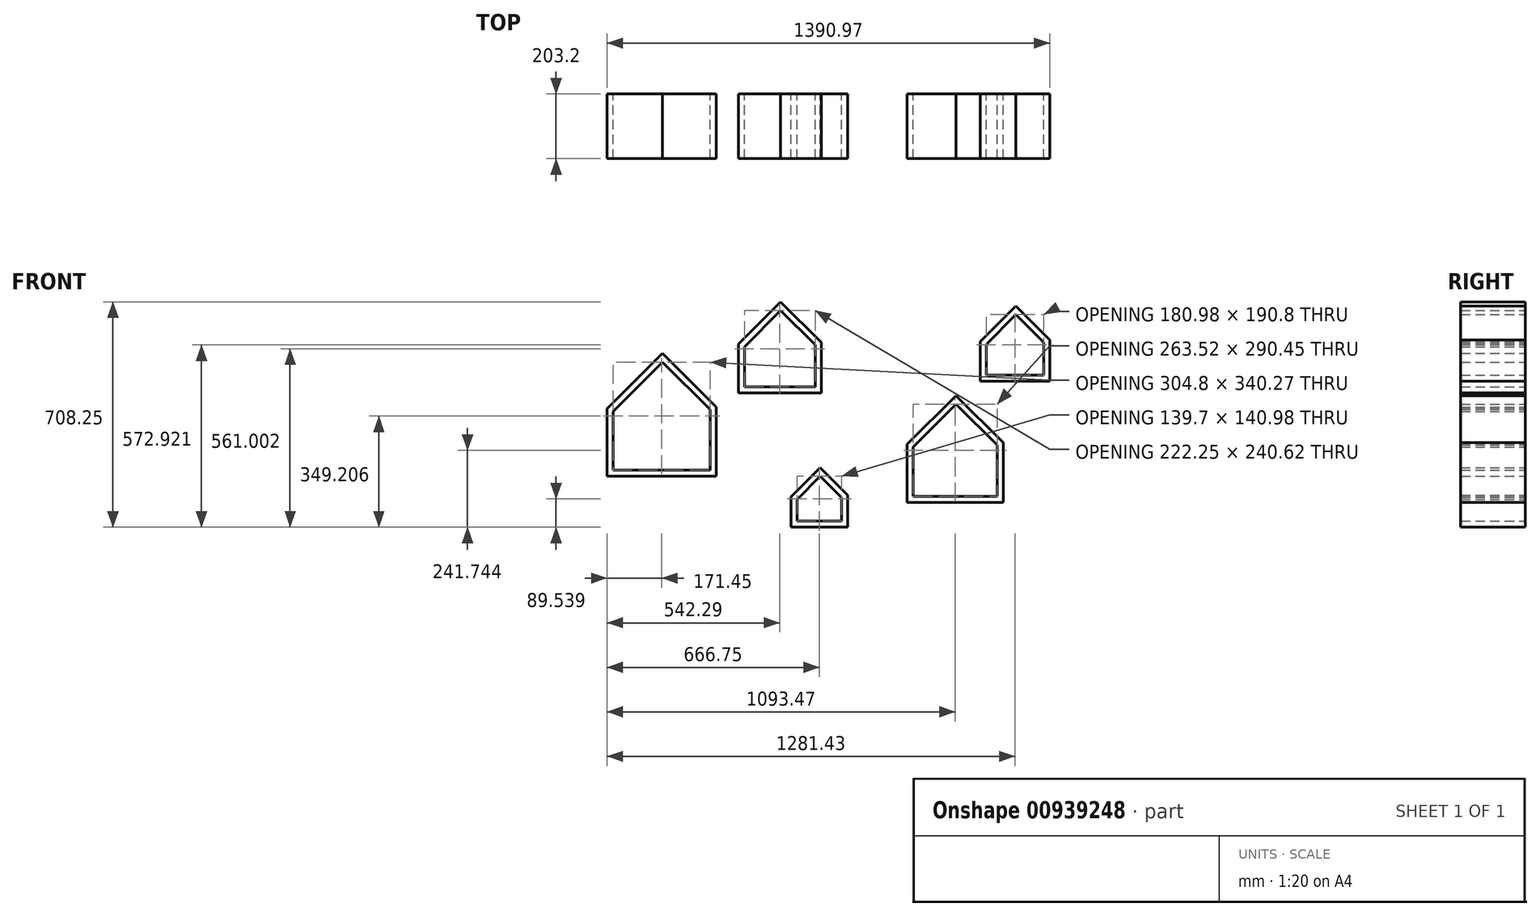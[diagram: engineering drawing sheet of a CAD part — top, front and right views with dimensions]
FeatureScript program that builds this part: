
annotation { "Feature Type Name" : "Feature", "Feature Type Description" : "" }
export const myFeature = defineFeature(function(context is Context, id is Id, definition is map)
    precondition{}
    {
        {
            var Q0;
            Q0=qCreatedBy(makeId("Front.planeOp"),FACE);
            var sketch = newSketch(context, id + "F0", { "sketchPlane" : qUnion([Q0])});
            skLineSegment(sketch, "E0.left", {"start": v(-274.9, 280.82) * mm, "end": v(-274.9, 95.58) * mm});
            skLineSegment(sketch, "E0.right", {"start": v(29.9, 286.08) * mm, "end": v(29.9, 95.58) * mm});
            skLineSegment(sketch, "E1", {"start": v(-119.86, 435.85) * mm, "end": v(-274.9, 280.82) * mm});
            skLineSegment(sketch, "E2", {"start": v(29.9, 286.08) * mm, "end": v(-119.86, 435.85) * mm});
            skPoint(sketch, "E3.start.orphan", {"position": v(-122.5, 283.45) * mm});
            skLineSegment(sketch, "E4", {"start": v(-274.9, 95.58) * mm, "end": v(29.9, 95.58) * mm});
            skLineSegment(sketch, "E5.0", {"start": v(48.96, 293.97) * mm, "end": v(48.96, 76.53) * mm});
            skLineSegment(sketch, "E5.1", {"start": v(-293.94, 76.53) * mm, "end": v(48.96, 76.53) * mm});
            skLineSegment(sketch, "E5.2", {"start": v(48.96, 293.97) * mm, "end": v(-119.86, 462.8) * mm});
            skLineSegment(sketch, "E5.3", {"start": v(-119.86, 462.8) * mm, "end": v(-293.94, 288.71) * mm});
            skLineSegment(sketch, "E5.4", {"start": v(-293.94, 288.71) * mm, "end": v(-293.94, 76.53) * mm});
            skLineSegment(sketch, "E6.0", {"start": v(-119.86, 433.6) * mm, "end": v(-273.3, 280.16) * mm});
            skLineSegment(sketch, "E6.1", {"start": v(28.32, 285.42) * mm, "end": v(-119.86, 433.6) * mm});
            skLineSegment(sketch, "E6.2", {"start": v(-273.3, 280.16) * mm, "end": v(-273.3, 97.17) * mm});
            skLineSegment(sketch, "E6.3", {"start": v(-273.3, 97.17) * mm, "end": v(28.32, 97.17) * mm});
            skLineSegment(sketch, "E6.4", {"start": v(28.32, 285.42) * mm, "end": v(28.32, 97.17) * mm});
            skLineSegment(sketch, "E7.0", {"start": v(-119.86, 406.66) * mm, "end": v(-254.25, 272.27) * mm});
            skLineSegment(sketch, "E7.1", {"start": v(9.27, 277.53) * mm, "end": v(-119.86, 406.66) * mm});
            skLineSegment(sketch, "E7.2", {"start": v(-254.25, 272.27) * mm, "end": v(-254.25, 116.22) * mm});
            skLineSegment(sketch, "E7.3", {"start": v(-254.25, 116.22) * mm, "end": v(9.27, 116.22) * mm});
            skLineSegment(sketch, "E7.4", {"start": v(9.27, 277.53) * mm, "end": v(9.27, 116.22) * mm});
            skLineSegment(sketch, "E8.0", {"start": v(-252.67, 271.61) * mm, "end": v(-252.67, 117.8) * mm});
            skLineSegment(sketch, "E8.1", {"start": v(-119.86, 404.42) * mm, "end": v(-252.67, 271.61) * mm});
            skLineSegment(sketch, "E8.2", {"start": v(-252.67, 117.8) * mm, "end": v(7.68, 117.8) * mm});
            skLineSegment(sketch, "E8.3", {"start": v(7.68, 276.87) * mm, "end": v(7.68, 117.8) * mm});
            skLineSegment(sketch, "E8.4", {"start": v(7.68, 276.87) * mm, "end": v(-119.86, 404.42) * mm});
            skLineSegment(sketch, "E9.0", {"start": v(-233.62, 263.72) * mm, "end": v(-233.62, 136.86) * mm});
            skLineSegment(sketch, "E9.1", {"start": v(-119.86, 377.48) * mm, "end": v(-233.62, 263.72) * mm});
            skLineSegment(sketch, "E9.2", {"start": v(-233.62, 136.86) * mm, "end": v(-11.37, 136.86) * mm});
            skLineSegment(sketch, "E9.3", {"start": v(-11.37, 268.98) * mm, "end": v(-11.37, 136.86) * mm});
            skLineSegment(sketch, "E9.4", {"start": v(-11.37, 268.98) * mm, "end": v(-119.86, 377.48) * mm});
            skLineSegment(sketch, "E10.0", {"start": v(-232.03, 263.07) * mm, "end": v(-232.03, 138.44) * mm});
            skLineSegment(sketch, "E10.1", {"start": v(-119.86, 375.23) * mm, "end": v(-232.03, 263.07) * mm});
            skLineSegment(sketch, "E10.2", {"start": v(-232.03, 138.44) * mm, "end": v(-12.95, 138.44) * mm});
            skLineSegment(sketch, "E10.3", {"start": v(-12.95, 268.33) * mm, "end": v(-12.95, 138.44) * mm});
            skLineSegment(sketch, "E10.4", {"start": v(-12.95, 268.33) * mm, "end": v(-119.86, 375.23) * mm});
            skLineSegment(sketch, "E11.0", {"start": v(-212.98, 255.18) * mm, "end": v(-212.98, 157.5) * mm});
            skLineSegment(sketch, "E11.1", {"start": v(-119.86, 348.3) * mm, "end": v(-212.98, 255.18) * mm});
            skLineSegment(sketch, "E11.2", {"start": v(-212.98, 157.5) * mm, "end": v(-32, 157.5) * mm});
            skLineSegment(sketch, "E11.3", {"start": v(-32, 260.44) * mm, "end": v(-32, 157.5) * mm});
            skLineSegment(sketch, "E11.4", {"start": v(-32, 260.44) * mm, "end": v(-119.86, 348.3) * mm});
            skLineSegment(sketch, "E12.0", {"start": v(-211.4, 254.52) * mm, "end": v(-211.4, 159.08) * mm});
            skLineSegment(sketch, "E12.1", {"start": v(-119.86, 346.05) * mm, "end": v(-211.4, 254.52) * mm});
            skLineSegment(sketch, "E12.2", {"start": v(-211.4, 159.08) * mm, "end": v(-33.6, 159.08) * mm});
            skLineSegment(sketch, "E12.3", {"start": v(-33.6, 259.78) * mm, "end": v(-33.6, 159.08) * mm});
            skLineSegment(sketch, "E12.4", {"start": v(-33.6, 259.78) * mm, "end": v(-119.86, 346.05) * mm});
            skLineSegment(sketch, "E13.0", {"start": v(-192.34, 246.63) * mm, "end": v(-192.34, 178.13) * mm});
            skLineSegment(sketch, "E13.1", {"start": v(-119.86, 319.1) * mm, "end": v(-192.34, 246.63) * mm});
            skLineSegment(sketch, "E13.2", {"start": v(-192.34, 178.13) * mm, "end": v(-52.64, 178.13) * mm});
            skLineSegment(sketch, "E13.3", {"start": v(-52.64, 251.89) * mm, "end": v(-52.64, 178.13) * mm});
            skLineSegment(sketch, "E13.4", {"start": v(-52.64, 251.89) * mm, "end": v(-119.86, 319.1) * mm});
            skSolve(sketch);
        }
        {
            var Q0;
            Q0=makeQuery(id+"F0.imprint","IMPRINT",FACE,{"disambiguationData":[TD([[makeQuery(id+"F0.imprint","IMPRINT",EDGE,{"derivedFrom":sQuery(id+"F0.wireOp",EDGE,"E0.left")}),-1.0]])]});
            var Q1;
            Q1=makeQuery(id+"F0.imprint","IMPRINT",FACE,{"disambiguationData":[TD([[makeQuery(id+"F0.imprint","IMPRINT",EDGE,{"derivedFrom":sQuery(id+"F0.wireOp",EDGE,"E6.0")}),1.0]])]});
            var Q2;
            Q2=makeQuery(id+"F0.imprint","IMPRINT",FACE,{"disambiguationData":[TD([[makeQuery(id+"F0.imprint","IMPRINT",EDGE,{"derivedFrom":sQuery(id+"F0.wireOp",EDGE,"E8.0")}),1.0]])]});
            var Q3;
            Q3=makeQuery(id+"F0.imprint","IMPRINT",FACE,{"disambiguationData":[TD([[makeQuery(id+"F0.imprint","IMPRINT",EDGE,{"derivedFrom":sQuery(id+"F0.wireOp",EDGE,"E10.0")}),1.0]])]});
            var Q4;
            Q4=makeQuery(id+"F0.imprint","IMPRINT",FACE,{"disambiguationData":[TD([[makeQuery(id+"F0.imprint","IMPRINT",EDGE,{"derivedFrom":sQuery(id+"F0.wireOp",EDGE,"E12.0")}),1.0]])]});
            extrude(context, id + "F1", {"entities" : qUnion([Q0, Q1, Q2, Q3, Q4]), "depth" : 203.2 * mm, "offsetDistance" : 25.4 * mm});
        }
        {
            var Q0;
            Q0=makeQuery(id+"F1.opExtrude","CAP_EDGE",EDGE,{"disambiguationData":[OSD([sQuery(id+"F0.wireOp",EDGE,"E6.3")])],"isStart":false});
            cPoint(context, id + "F2", {"entities" : qUnion([Q0]), "parameter" : 0.5});
        }
        {
            var Q0;
            Q0=makeQuery(id+"F1.opExtrude","CAP_EDGE",EDGE,{"disambiguationData":[OSD([sQuery(id+"F0.wireOp",EDGE,"E4")])],"isStart":false});
            cPoint(context, id + "F3", {"entities" : qUnion([Q0]), "parameter" : 0.5});
        }
        {
            var Q0;
            Q0=makeQuery(id+"F1.opExtrude","SWEPT_BODY",BODY,{"disambiguationData":[OSD([sQuery(id+"F0.wireOp",EDGE,"E6.0"),sQuery(id+"F0.wireOp",EDGE,"E6.1"),sQuery(id+"F0.wireOp",EDGE,"E6.2"),sQuery(id+"F0.wireOp",EDGE,"E6.3"),sQuery(id+"F0.wireOp",EDGE,"E6.4"),sQuery(id+"F0.wireOp",EDGE,"E7.0"),sQuery(id+"F0.wireOp",EDGE,"E7.1"),sQuery(id+"F0.wireOp",EDGE,"E7.2"),sQuery(id+"F0.wireOp",EDGE,"E7.3"),sQuery(id+"F0.wireOp",EDGE,"E7.4")])]});
            var Q1;
            Q1 = qCreatedBy(id + "F2" ,VERTEX);
            var Q2;
            Q2 = qCreatedBy(id + "F3" ,VERTEX);
            transform(context, id + "F4", {"entities" : qUnion([Q0]), "transformType" : TransformType.TRANSLATION_ENTITY, "oppositeDirectionEntity" : false, "transformLine" : qUnion([Q1, Q2]), "makeCopy" : false});
        }
        {
            var Q0;
            Q0=makeQuery(id+"F1.opExtrude","CAP_EDGE",EDGE,{"disambiguationData":[OSD([sQuery(id+"F0.wireOp",EDGE,"E8.2")])],"isStart":false});
            cPoint(context, id + "F5", {"entities" : qUnion([Q0]), "parameter" : 0.5});
        }
        {
            var Q0;
            Q0=makeQuery(id+"F1.opExtrude","CAP_EDGE",EDGE,{"disambiguationData":[OSD([sQuery(id+"F0.wireOp",EDGE,"E7.3")])],"isStart":false});
            cPoint(context, id + "F6", {"entities" : qUnion([Q0]), "parameter" : 0.5});
        }
        {
            var Q0;
            Q0=makeQuery(id+"F1.opExtrude","SWEPT_BODY",BODY,{"disambiguationData":[OSD([sQuery(id+"F0.wireOp",EDGE,"E8.0"),sQuery(id+"F0.wireOp",EDGE,"E8.1"),sQuery(id+"F0.wireOp",EDGE,"E8.2"),sQuery(id+"F0.wireOp",EDGE,"E8.3"),sQuery(id+"F0.wireOp",EDGE,"E8.4"),sQuery(id+"F0.wireOp",EDGE,"E9.0"),sQuery(id+"F0.wireOp",EDGE,"E9.1"),sQuery(id+"F0.wireOp",EDGE,"E9.2"),sQuery(id+"F0.wireOp",EDGE,"E9.3"),sQuery(id+"F0.wireOp",EDGE,"E9.4")])]});
            var Q1;
            Q1 = qCreatedBy(id + "F5" ,VERTEX);
            var Q2;
            Q2 = qCreatedBy(id + "F6" ,VERTEX);
            transform(context, id + "F7", {"entities" : qUnion([Q0]), "transformType" : TransformType.TRANSLATION_ENTITY, "oppositeDirectionEntity" : false, "transformLine" : qUnion([Q1, Q2]), "makeCopy" : false});
        }
        {
            var Q0;
            Q0=makeQuery(id+"F1.opExtrude","CAP_EDGE",EDGE,{"disambiguationData":[OSD([sQuery(id+"F0.wireOp",EDGE,"E10.2")])],"isStart":false});
            cPoint(context, id + "F8", {"entities" : qUnion([Q0]), "parameter" : 0.5});
        }
        {
            var Q0;
            Q0=makeQuery(id+"F1.opExtrude","CAP_EDGE",EDGE,{"disambiguationData":[OSD([sQuery(id+"F0.wireOp",EDGE,"E9.2")])],"isStart":false});
            cPoint(context, id + "F9", {"entities" : qUnion([Q0]), "parameter" : 0.5});
        }
        {
            var Q0;
            Q0=makeQuery(id+"F1.opExtrude","SWEPT_BODY",BODY,{"disambiguationData":[OSD([sQuery(id+"F0.wireOp",EDGE,"E10.0"),sQuery(id+"F0.wireOp",EDGE,"E10.1"),sQuery(id+"F0.wireOp",EDGE,"E10.2"),sQuery(id+"F0.wireOp",EDGE,"E10.3"),sQuery(id+"F0.wireOp",EDGE,"E10.4"),sQuery(id+"F0.wireOp",EDGE,"E11.0"),sQuery(id+"F0.wireOp",EDGE,"E11.1"),sQuery(id+"F0.wireOp",EDGE,"E11.2"),sQuery(id+"F0.wireOp",EDGE,"E11.3"),sQuery(id+"F0.wireOp",EDGE,"E11.4")])]});
            var Q1;
            Q1 = qCreatedBy(id + "F8" ,VERTEX);
            var Q2;
            Q2 = qCreatedBy(id + "F9" ,VERTEX);
            transform(context, id + "F10", {"entities" : qUnion([Q0]), "transformType" : TransformType.TRANSLATION_ENTITY, "oppositeDirectionEntity" : false, "transformLine" : qUnion([Q1, Q2]), "makeCopy" : false});
        }
        {
            var Q0;
            Q0=makeQuery(id+"F1.opExtrude","CAP_EDGE",EDGE,{"disambiguationData":[OSD([sQuery(id+"F0.wireOp",EDGE,"E12.2")])],"isStart":false});
            cPoint(context, id + "F11", {"entities" : qUnion([Q0]), "parameter" : 0.5});
        }
        {
            var Q0;
            Q0=makeQuery(id+"F1.opExtrude","CAP_EDGE",EDGE,{"disambiguationData":[OSD([sQuery(id+"F0.wireOp",EDGE,"E11.2")])],"isStart":false});
            cPoint(context, id + "F12", {"entities" : qUnion([Q0]), "parameter" : 0.5});
        }
        {
            var Q0;
            Q0=makeQuery(id+"F1.opExtrude","SWEPT_BODY",BODY,{"disambiguationData":[OSD([sQuery(id+"F0.wireOp",EDGE,"E12.0"),sQuery(id+"F0.wireOp",EDGE,"E12.1"),sQuery(id+"F0.wireOp",EDGE,"E12.2"),sQuery(id+"F0.wireOp",EDGE,"E12.3"),sQuery(id+"F0.wireOp",EDGE,"E12.4"),sQuery(id+"F0.wireOp",EDGE,"E13.0"),sQuery(id+"F0.wireOp",EDGE,"E13.1"),sQuery(id+"F0.wireOp",EDGE,"E13.2"),sQuery(id+"F0.wireOp",EDGE,"E13.3"),sQuery(id+"F0.wireOp",EDGE,"E13.4")])]});
            var Q1;
            Q1 = qCreatedBy(id + "F11" ,VERTEX);
            var Q2;
            Q2 = qCreatedBy(id + "F12" ,VERTEX);
            transform(context, id + "F13", {"entities" : qUnion([Q0]), "transformType" : TransformType.TRANSLATION_ENTITY, "oppositeDirectionEntity" : false, "transformLine" : qUnion([Q1, Q2]), "makeCopy" : false});
        }
        {
            var Q0;
            Q0=makeQuery(id+"F1.opExtrude","SWEPT_BODY",BODY,{"disambiguationData":[OSD([sQuery(id+"F0.wireOp",EDGE,"E12.0"),sQuery(id+"F0.wireOp",EDGE,"E12.1"),sQuery(id+"F0.wireOp",EDGE,"E12.2"),sQuery(id+"F0.wireOp",EDGE,"E12.3"),sQuery(id+"F0.wireOp",EDGE,"E12.4"),sQuery(id+"F0.wireOp",EDGE,"E13.0"),sQuery(id+"F0.wireOp",EDGE,"E13.1"),sQuery(id+"F0.wireOp",EDGE,"E13.2"),sQuery(id+"F0.wireOp",EDGE,"E13.3"),sQuery(id+"F0.wireOp",EDGE,"E13.4")])]});
            transform(context, id + "F14", {"entities" : qUnion([Q0]), "transformType" : TransformType.TRANSLATION_3D, "dx" : 546.1 * mm, "dy" : 0 * mm, "dz" : 208.28 * mm, "makeCopy" : false});
        }
        {
            var Q0;
            Q0=makeQuery(id+"F1.opExtrude","SWEPT_BODY",BODY,{"disambiguationData":[OSD([sQuery(id+"F0.wireOp",EDGE,"E10.0"),sQuery(id+"F0.wireOp",EDGE,"E10.1"),sQuery(id+"F0.wireOp",EDGE,"E10.2"),sQuery(id+"F0.wireOp",EDGE,"E10.3"),sQuery(id+"F0.wireOp",EDGE,"E10.4"),sQuery(id+"F0.wireOp",EDGE,"E11.0"),sQuery(id+"F0.wireOp",EDGE,"E11.1"),sQuery(id+"F0.wireOp",EDGE,"E11.2"),sQuery(id+"F0.wireOp",EDGE,"E11.3"),sQuery(id+"F0.wireOp",EDGE,"E11.4")])]});
            transform(context, id + "F15", {"entities" : qUnion([Q0]), "transformType" : TransformType.TRANSLATION_3D, "dx" : 454.66 * mm, "dy" : 0 * mm, "dz" : -302.26 * mm, "makeCopy" : false});
        }
        {
            var Q0;
            Q0=makeQuery(id+"F1.opExtrude","SWEPT_BODY",BODY,{"disambiguationData":[OSD([sQuery(id+"F0.wireOp",EDGE,"E8.0"),sQuery(id+"F0.wireOp",EDGE,"E8.1"),sQuery(id+"F0.wireOp",EDGE,"E8.2"),sQuery(id+"F0.wireOp",EDGE,"E8.3"),sQuery(id+"F0.wireOp",EDGE,"E8.4"),sQuery(id+"F0.wireOp",EDGE,"E9.0"),sQuery(id+"F0.wireOp",EDGE,"E9.1"),sQuery(id+"F0.wireOp",EDGE,"E9.2"),sQuery(id+"F0.wireOp",EDGE,"E9.3"),sQuery(id+"F0.wireOp",EDGE,"E9.4")])]});
            transform(context, id + "F16", {"entities" : qUnion([Q0]), "transformType" : TransformType.TRANSLATION_3D, "dx" : 756.92 * mm, "dy" : 0 * mm, "dz" : 0 * mm, "makeCopy" : false});
        }
        {
            var Q0;
            Q0=makeQuery(id+"F1.opExtrude","SWEPT_BODY",BODY,{"disambiguationData":[OSD([sQuery(id+"F0.wireOp",EDGE,"E6.0"),sQuery(id+"F0.wireOp",EDGE,"E6.1"),sQuery(id+"F0.wireOp",EDGE,"E6.2"),sQuery(id+"F0.wireOp",EDGE,"E6.3"),sQuery(id+"F0.wireOp",EDGE,"E6.4"),sQuery(id+"F0.wireOp",EDGE,"E7.0"),sQuery(id+"F0.wireOp",EDGE,"E7.1"),sQuery(id+"F0.wireOp",EDGE,"E7.2"),sQuery(id+"F0.wireOp",EDGE,"E7.3"),sQuery(id+"F0.wireOp",EDGE,"E7.4")])]});
            transform(context, id + "F17", {"entities" : qUnion([Q0]), "transformType" : TransformType.TRANSLATION_3D, "dx" : -457.2 * mm, "dy" : 0 * mm, "dz" : 162.56 * mm, "makeCopy" : false});
        }
        {
            var Q0;
            Q0=makeQuery(id+"F1.opExtrude","SWEPT_BODY",BODY,{"disambiguationData":[OSD([sQuery(id+"F0.wireOp",EDGE,"E6.0"),sQuery(id+"F0.wireOp",EDGE,"E6.1"),sQuery(id+"F0.wireOp",EDGE,"E6.2"),sQuery(id+"F0.wireOp",EDGE,"E6.3"),sQuery(id+"F0.wireOp",EDGE,"E6.4"),sQuery(id+"F0.wireOp",EDGE,"E7.0"),sQuery(id+"F0.wireOp",EDGE,"E7.1"),sQuery(id+"F0.wireOp",EDGE,"E7.2"),sQuery(id+"F0.wireOp",EDGE,"E7.3"),sQuery(id+"F0.wireOp",EDGE,"E7.4")])]});
            transform(context, id + "F18", {"entities" : qUnion([Q0]), "transformType" : TransformType.TRANSLATION_3D, "dx" : 1379.22 * mm, "dy" : 0 * mm, "dz" : -264.16 * mm, "makeCopy" : false});
        }
        {
            var Q0;
            Q0=makeQuery(id+"F1.opExtrude","SWEPT_BODY",BODY,{"disambiguationData":[OSD([sQuery(id+"F0.wireOp",EDGE,"E10.0"),sQuery(id+"F0.wireOp",EDGE,"E10.1"),sQuery(id+"F0.wireOp",EDGE,"E10.2"),sQuery(id+"F0.wireOp",EDGE,"E10.3"),sQuery(id+"F0.wireOp",EDGE,"E10.4"),sQuery(id+"F0.wireOp",EDGE,"E11.0"),sQuery(id+"F0.wireOp",EDGE,"E11.1"),sQuery(id+"F0.wireOp",EDGE,"E11.2"),sQuery(id+"F0.wireOp",EDGE,"E11.3"),sQuery(id+"F0.wireOp",EDGE,"E11.4")])]});
            transform(context, id + "F19", {"entities" : qUnion([Q0]), "transformType" : TransformType.TRANSLATION_3D, "dx" : -119.38 * mm, "dy" : 0 * mm, "dz" : 33.02 * mm, "makeCopy" : false});
        }
        {
            var Q0;
            Q0=makeQuery(id+"F1.opExtrude","SWEPT_BODY",BODY,{"disambiguationData":[OSD([sQuery(id+"F0.wireOp",EDGE,"E12.0"),sQuery(id+"F0.wireOp",EDGE,"E12.1"),sQuery(id+"F0.wireOp",EDGE,"E12.2"),sQuery(id+"F0.wireOp",EDGE,"E12.3"),sQuery(id+"F0.wireOp",EDGE,"E12.4"),sQuery(id+"F0.wireOp",EDGE,"E13.0"),sQuery(id+"F0.wireOp",EDGE,"E13.1"),sQuery(id+"F0.wireOp",EDGE,"E13.2"),sQuery(id+"F0.wireOp",EDGE,"E13.3"),sQuery(id+"F0.wireOp",EDGE,"E13.4")])]});
            transform(context, id + "F20", {"entities" : qUnion([Q0]), "transformType" : TransformType.TRANSLATION_3D, "dx" : 157.48 * mm, "dy" : 0 * mm, "dz" : 0 * mm, "makeCopy" : false});
        }
        {
            var Q0;
            Q0=makeQuery(id+"F1.opExtrude","SWEPT_BODY",BODY,{"disambiguationData":[OSD([sQuery(id+"F0.wireOp",EDGE,"E8.0"),sQuery(id+"F0.wireOp",EDGE,"E8.1"),sQuery(id+"F0.wireOp",EDGE,"E8.2"),sQuery(id+"F0.wireOp",EDGE,"E8.3"),sQuery(id+"F0.wireOp",EDGE,"E8.4"),sQuery(id+"F0.wireOp",EDGE,"E9.0"),sQuery(id+"F0.wireOp",EDGE,"E9.1"),sQuery(id+"F0.wireOp",EDGE,"E9.2"),sQuery(id+"F0.wireOp",EDGE,"E9.3"),sQuery(id+"F0.wireOp",EDGE,"E9.4")])]});
            transform(context, id + "F21", {"entities" : qUnion([Q0]), "transformType" : TransformType.TRANSLATION_3D, "dx" : -386.08 * mm, "dy" : 0 * mm, "dz" : 223.52 * mm, "makeCopy" : false});
        }
        {
            var Q0;
            Q0=makeQuery(id+"F1.opExtrude","SWEPT_BODY",BODY,{"disambiguationData":[OSD([sQuery(id+"F0.wireOp",EDGE,"E12.0"),sQuery(id+"F0.wireOp",EDGE,"E12.1"),sQuery(id+"F0.wireOp",EDGE,"E12.2"),sQuery(id+"F0.wireOp",EDGE,"E12.3"),sQuery(id+"F0.wireOp",EDGE,"E12.4"),sQuery(id+"F0.wireOp",EDGE,"E13.0"),sQuery(id+"F0.wireOp",EDGE,"E13.1"),sQuery(id+"F0.wireOp",EDGE,"E13.2"),sQuery(id+"F0.wireOp",EDGE,"E13.3"),sQuery(id+"F0.wireOp",EDGE,"E13.4")])]});
            transform(context, id + "F22", {"entities" : qUnion([Q0]), "transformType" : TransformType.TRANSLATION_3D, "dx" : -208.28 * mm, "dy" : 0 * mm, "dz" : -340.36 * mm, "makeCopy" : false});
        }
        {
            var Q0;
            Q0=makeQuery(id+"F1.opExtrude","SWEPT_BODY",BODY,{"disambiguationData":[OSD([sQuery(id+"F0.wireOp",EDGE,"E10.0"),sQuery(id+"F0.wireOp",EDGE,"E10.1"),sQuery(id+"F0.wireOp",EDGE,"E10.2"),sQuery(id+"F0.wireOp",EDGE,"E10.3"),sQuery(id+"F0.wireOp",EDGE,"E10.4"),sQuery(id+"F0.wireOp",EDGE,"E11.0"),sQuery(id+"F0.wireOp",EDGE,"E11.1"),sQuery(id+"F0.wireOp",EDGE,"E11.2"),sQuery(id+"F0.wireOp",EDGE,"E11.3"),sQuery(id+"F0.wireOp",EDGE,"E11.4")])]});
            transform(context, id + "F23", {"entities" : qUnion([Q0]), "transformType" : TransformType.TRANSLATION_3D, "dx" : 774.7 * mm, "dy" : 0 * mm, "dz" : 510.54 * mm, "makeCopy" : false});
        }
        {
            var Q0;
            Q0=makeQuery(id+"F1.opExtrude","SWEPT_BODY",BODY,{"disambiguationData":[OSD([sQuery(id+"F0.wireOp",EDGE,"E12.0"),sQuery(id+"F0.wireOp",EDGE,"E12.1"),sQuery(id+"F0.wireOp",EDGE,"E12.2"),sQuery(id+"F0.wireOp",EDGE,"E12.3"),sQuery(id+"F0.wireOp",EDGE,"E12.4"),sQuery(id+"F0.wireOp",EDGE,"E13.0"),sQuery(id+"F0.wireOp",EDGE,"E13.1"),sQuery(id+"F0.wireOp",EDGE,"E13.2"),sQuery(id+"F0.wireOp",EDGE,"E13.3"),sQuery(id+"F0.wireOp",EDGE,"E13.4")])]});
            transform(context, id + "F24", {"entities" : qUnion([Q0]), "transformType" : TransformType.TRANSLATION_3D, "dx" : 0 * mm, "dy" : 0 * mm, "dz" : -104.14 * mm, "makeCopy" : false});
        }
        {
            var Q0;
            Q0=makeQuery(id+"F1.opExtrude","SWEPT_BODY",BODY,{"disambiguationData":[OSD([sQuery(id+"F0.wireOp",EDGE,"E6.0"),sQuery(id+"F0.wireOp",EDGE,"E6.1"),sQuery(id+"F0.wireOp",EDGE,"E6.2"),sQuery(id+"F0.wireOp",EDGE,"E6.3"),sQuery(id+"F0.wireOp",EDGE,"E6.4"),sQuery(id+"F0.wireOp",EDGE,"E7.0"),sQuery(id+"F0.wireOp",EDGE,"E7.1"),sQuery(id+"F0.wireOp",EDGE,"E7.2"),sQuery(id+"F0.wireOp",EDGE,"E7.3"),sQuery(id+"F0.wireOp",EDGE,"E7.4")])]});
            var Q1;
            Q1=makeQuery(id+"F1.opExtrude","SWEPT_BODY",BODY,{"disambiguationData":[OSD([sQuery(id+"F0.wireOp",EDGE,"E10.0"),sQuery(id+"F0.wireOp",EDGE,"E10.1"),sQuery(id+"F0.wireOp",EDGE,"E10.2"),sQuery(id+"F0.wireOp",EDGE,"E10.3"),sQuery(id+"F0.wireOp",EDGE,"E10.4"),sQuery(id+"F0.wireOp",EDGE,"E11.0"),sQuery(id+"F0.wireOp",EDGE,"E11.1"),sQuery(id+"F0.wireOp",EDGE,"E11.2"),sQuery(id+"F0.wireOp",EDGE,"E11.3"),sQuery(id+"F0.wireOp",EDGE,"E11.4")])]});
            var Q2;
            Q2=makeQuery(id+"F1.opExtrude","SWEPT_BODY",BODY,{"disambiguationData":[OSD([sQuery(id+"F0.wireOp",EDGE,"E0.left"),sQuery(id+"F0.wireOp",EDGE,"E0.right"),sQuery(id+"F0.wireOp",EDGE,"E1"),sQuery(id+"F0.wireOp",EDGE,"E2"),sQuery(id+"F0.wireOp",EDGE,"E4"),sQuery(id+"F0.wireOp",EDGE,"E5.0"),sQuery(id+"F0.wireOp",EDGE,"E5.1"),sQuery(id+"F0.wireOp",EDGE,"E5.2"),sQuery(id+"F0.wireOp",EDGE,"E5.3"),sQuery(id+"F0.wireOp",EDGE,"E5.4")])]});
            var Q3;
            Q3=makeQuery(id+"F1.opExtrude","SWEPT_BODY",BODY,{"disambiguationData":[OSD([sQuery(id+"F0.wireOp",EDGE,"E12.0"),sQuery(id+"F0.wireOp",EDGE,"E12.1"),sQuery(id+"F0.wireOp",EDGE,"E12.2"),sQuery(id+"F0.wireOp",EDGE,"E12.3"),sQuery(id+"F0.wireOp",EDGE,"E12.4"),sQuery(id+"F0.wireOp",EDGE,"E13.0"),sQuery(id+"F0.wireOp",EDGE,"E13.1"),sQuery(id+"F0.wireOp",EDGE,"E13.2"),sQuery(id+"F0.wireOp",EDGE,"E13.3"),sQuery(id+"F0.wireOp",EDGE,"E13.4")])]});
            var Q4;
            Q4=makeQuery(id+"F1.opExtrude","SWEPT_BODY",BODY,{"disambiguationData":[OSD([sQuery(id+"F0.wireOp",EDGE,"E8.0"),sQuery(id+"F0.wireOp",EDGE,"E8.1"),sQuery(id+"F0.wireOp",EDGE,"E8.2"),sQuery(id+"F0.wireOp",EDGE,"E8.3"),sQuery(id+"F0.wireOp",EDGE,"E8.4"),sQuery(id+"F0.wireOp",EDGE,"E9.0"),sQuery(id+"F0.wireOp",EDGE,"E9.1"),sQuery(id+"F0.wireOp",EDGE,"E9.2"),sQuery(id+"F0.wireOp",EDGE,"E9.3"),sQuery(id+"F0.wireOp",EDGE,"E9.4")])]});
            transform(context, id + "F25", {"entities" : qUnion([Q0, Q1, Q2, Q3, Q4]), "transformType" : TransformType.TRANSLATION_3D, "dx" : 0 * mm, "dy" : 0 * mm, "dz" : 668.02 * mm, "makeCopy" : false});
        }
    });
